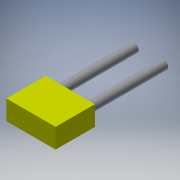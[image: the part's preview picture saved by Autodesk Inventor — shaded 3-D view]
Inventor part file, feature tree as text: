
AUTODESK INVENTOR PART (.ipt)
format: ipt  version: 2019 (Build 230136000, 136)  size: 121,344 bytes
history: native  units: mm
features: extrude x2, sketch x2
ambient origin geometry x8: Origin, YZ Plane, XZ Plane, XY Plane, X Axis, Y Axis, Z Axis, Center Point
bodies: Solid1 (feature_tree)
feature tree (4):
  extrude  "Extrusion1"  Depth=25.0mm
  extrude  "Extrusion2"  Depth=60.0mm
  sketch  "Sketch1"  dims[d0=10.0mm d1=25.0mm]
  sketch  "Sketch2"  dims[d2=2.5mm d3=7.5mm d4=20.0mm d5=0.0mm d6=4.5mm d7=5.0mm d8=5.0mm d9=5.0mm d10=5.0mm d11=60.0mm d12=0.0mm]
